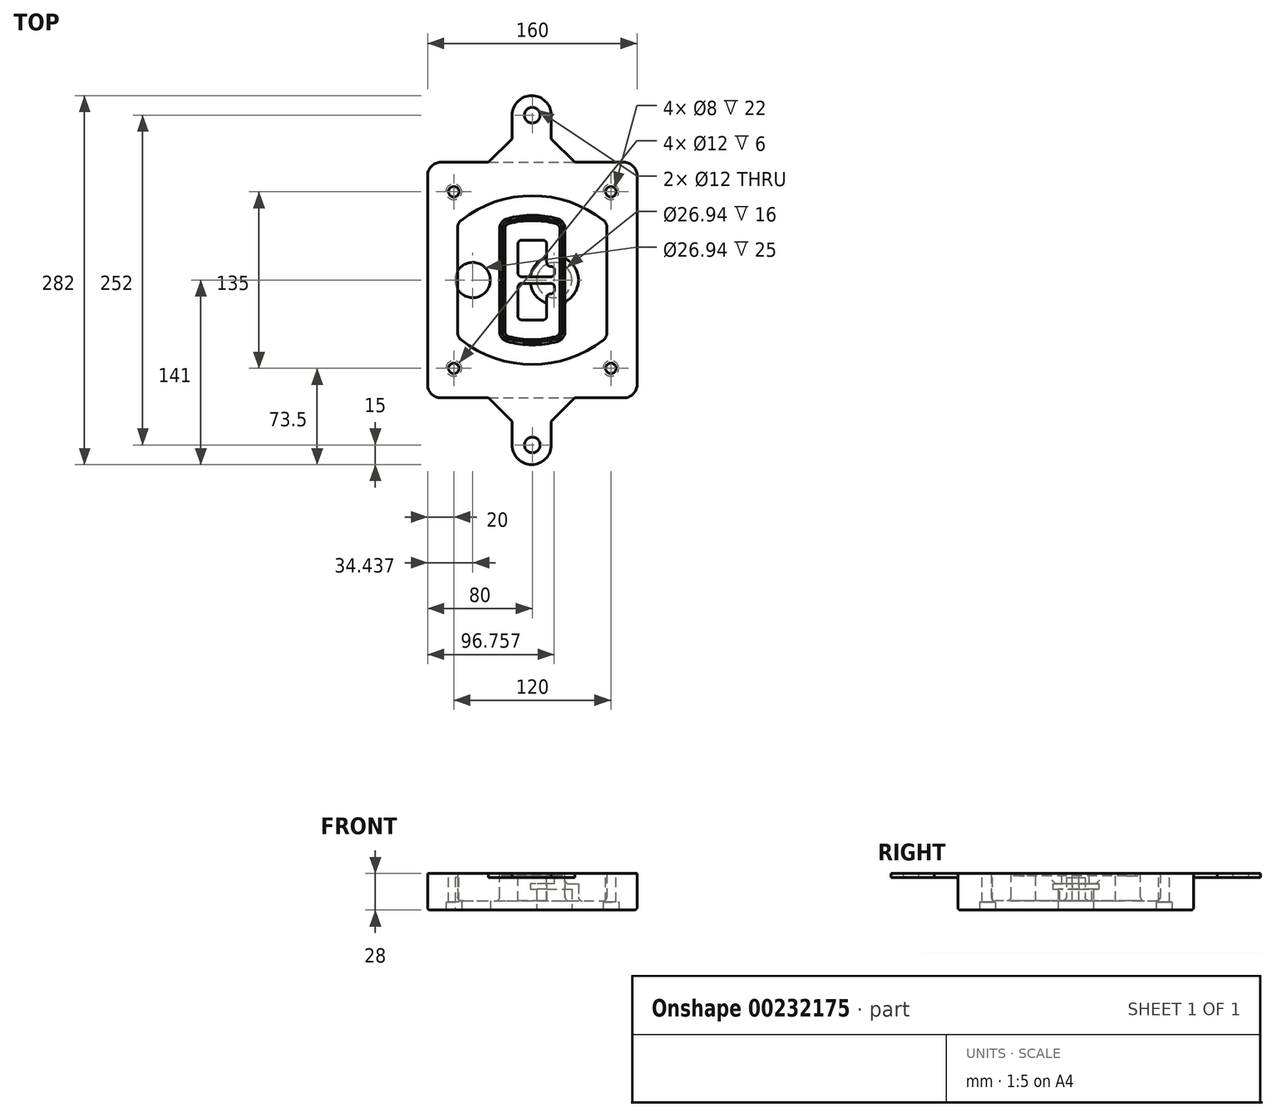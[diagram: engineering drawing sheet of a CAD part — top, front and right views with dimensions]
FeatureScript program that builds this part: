
annotation { "Feature Type Name" : "Feature", "Feature Type Description" : "" }
export const myFeature = defineFeature(function(context is Context, id is Id, definition is map)
    precondition{}
    {
        {
            var Q0;
            Q0=qCreatedBy(makeId("Top.planeOp"),FACE);
            var sketch = newSketch(context, id + "F0", { "sketchPlane" : qUnion([Q0])});
            skPoint(sketch, "E0.rect.middle", {"position": v(0, 0) * mm});
            skLineSegment(sketch, "E1.bottom", {"start": v(-70, -90) * mm, "end": v(70, -90) * mm});
            skLineSegment(sketch, "E1.top", {"start": v(-70, 90) * mm, "end": v(70, 90) * mm});
            skLineSegment(sketch, "E1.left", {"start": v(-80, -80) * mm, "end": v(-80, 80) * mm});
            skLineSegment(sketch, "E1.right", {"start": v(80, -80) * mm, "end": v(80, 80) * mm});
            skLineSegment(sketch, "E2", {"start": v(-80, 90) * mm, "end": v(80, -90) * mm, "construction": true});
            skLineSegment(sketch, "E3", {"start": v(80, 90) * mm, "end": v(-80, -90) * mm, "construction": true});
            skCircle(sketch, "E4", {"center": v(-60, 67.5) * mm, "radius": 4 * mm});
            skCircle(sketch, "E5", {"center": v(60, 67.5) * mm, "radius": 4 * mm});
            skCircle(sketch, "E6", {"center": v(60, -67.5) * mm, "radius": 4 * mm});
            skCircle(sketch, "E7", {"center": v(-60, -67.5) * mm, "radius": 4 * mm});
            skLineSegment(sketch, "E8", {"start": v(-60, 67.5) * mm, "end": v(60, 67.5) * mm, "construction": true});
            skLineSegment(sketch, "E9", {"start": v(60, 67.5) * mm, "end": v(60, -67.5) * mm, "construction": true});
            skLineSegment(sketch, "E10", {"start": v(60, -67.5) * mm, "end": v(-60, -67.5) * mm, "construction": true});
            skLineSegment(sketch, "E11", {"start": v(-60, -67.5) * mm, "end": v(-60, 67.5) * mm, "construction": true});
            skLineSegment(sketch, "E12", {"start": v(-60, 40.3) * mm, "end": v(-60, -40.3) * mm});
            skLineSegment(sketch, "E13", {"start": v(60, 40.3) * mm, "end": v(60, -40.3) * mm});
            skArc(sketch, "E14", {"start": v(56.15, 48.18) * mm, "mid": v(0, 67.5) * mm, "end": v(-56.15, 48.18) * mm});
            skArc(sketch, "E15", {"start": v(-56.15, -48.18) * mm, "mid": v(0, -67.5) * mm, "end": v(56.15, -48.18) * mm});
            skLineSegment(sketch, "E16", {"start": v(-60, 0) * mm, "end": v(60, 0) * mm, "construction": true});
            skPoint(sketch, "E17.visualSharp", {"position": v(-60, -45) * mm});
            skArc(sketch, "E17.filletArc", {"start": v(-60, -40.3) * mm, "mid": v(-58.99, -44.68) * mm, "end": v(-56.15, -48.18) * mm});
            skPoint(sketch, "E18.visualSharp", {"position": v(-60, 45) * mm});
            skArc(sketch, "E18.filletArc", {"start": v(-56.15, 48.18) * mm, "mid": v(-58.99, 44.68) * mm, "end": v(-60, 40.3) * mm});
            skPoint(sketch, "E19.visualSharp", {"position": v(60, 45) * mm});
            skArc(sketch, "E19.filletArc", {"start": v(60, 40.3) * mm, "mid": v(58.99, 44.68) * mm, "end": v(56.15, 48.18) * mm});
            skPoint(sketch, "E20.visualSharp", {"position": v(60, -45) * mm});
            skArc(sketch, "E20.filletArc", {"start": v(56.15, -48.18) * mm, "mid": v(58.99, -44.68) * mm, "end": v(60, -40.3) * mm});
            skPoint(sketch, "E21.visualSharp", {"position": v(-80, 90) * mm});
            skArc(sketch, "E21.filletArc", {"start": v(-70, 90) * mm, "mid": v(-77.07, 87.07) * mm, "end": v(-80, 80) * mm});
            skPoint(sketch, "E22.visualSharp", {"position": v(80, 90) * mm});
            skArc(sketch, "E22.filletArc", {"start": v(80, 80) * mm, "mid": v(77.07, 87.07) * mm, "end": v(70, 90) * mm});
            skPoint(sketch, "E23.visualSharp", {"position": v(80, -90) * mm});
            skArc(sketch, "E23.filletArc", {"start": v(70, -90) * mm, "mid": v(77.07, -87.07) * mm, "end": v(80, -80) * mm});
            skPoint(sketch, "E24.visualSharp", {"position": v(-80, -90) * mm});
            skArc(sketch, "E24.filletArc", {"start": v(-80, -80) * mm, "mid": v(-77.07, -87.07) * mm, "end": v(-70, -90) * mm});
            skArc(sketch, "E25.0", {"start": v(57, 40.3) * mm, "mid": v(56.3, 43.36) * mm, "end": v(54.3, 45.81) * mm});
            skLineSegment(sketch, "E25.1", {"start": v(57, 40.3) * mm, "end": v(57, -40.3) * mm});
            skArc(sketch, "E25.2", {"start": v(54.3, -45.81) * mm, "mid": v(56.3, -43.36) * mm, "end": v(57, -40.3) * mm});
            skArc(sketch, "E25.3", {"start": v(-54.3, -45.81) * mm, "mid": v(0, -64.5) * mm, "end": v(54.3, -45.81) * mm});
            skArc(sketch, "E25.4", {"start": v(-57, -40.3) * mm, "mid": v(-56.3, -43.36) * mm, "end": v(-54.3, -45.81) * mm});
            skArc(sketch, "E25.5", {"start": v(54.3, 45.81) * mm, "mid": v(0, 64.5) * mm, "end": v(-54.3, 45.81) * mm});
            skLineSegment(sketch, "E25.6", {"start": v(-57, 40.3) * mm, "end": v(-57, -40.3) * mm});
            skArc(sketch, "E25.7", {"start": v(-54.3, 45.81) * mm, "mid": v(-56.3, 43.36) * mm, "end": v(-57, 40.3) * mm});
            skArc(sketch, "E26.0", {"start": v(-58.62, 51.33) * mm, "mid": v(-62.58, 46.43) * mm, "end": v(-64, 40.3) * mm});
            skArc(sketch, "E26.1", {"start": v(58.62, 51.33) * mm, "mid": v(0, 71.5) * mm, "end": v(-58.62, 51.33) * mm});
            skArc(sketch, "E26.2", {"start": v(64, 40.3) * mm, "mid": v(62.58, 46.43) * mm, "end": v(58.62, 51.33) * mm});
            skLineSegment(sketch, "E26.3", {"start": v(64, 40.3) * mm, "end": v(64, -40.3) * mm});
            skArc(sketch, "E26.4", {"start": v(58.62, -51.33) * mm, "mid": v(62.58, -46.43) * mm, "end": v(64, -40.3) * mm});
            skLineSegment(sketch, "E26.5", {"start": v(-64, 40.3) * mm, "end": v(-64, -40.3) * mm});
            skArc(sketch, "E26.6", {"start": v(-58.62, -51.33) * mm, "mid": v(0, -71.5) * mm, "end": v(58.62, -51.33) * mm});
            skArc(sketch, "E26.7", {"start": v(-64, -40.3) * mm, "mid": v(-62.58, -46.43) * mm, "end": v(-58.62, -51.33) * mm});
            skSolve(sketch);
        }
        {
            var Q0;
            Q0=makeQuery(id+"F0.imprint","IMPRINT",FACE,{"disambiguationData":[TD([[makeQuery(id+"F0.imprint","IMPRINT",EDGE,{"derivedFrom":sQuery(id+"F0.wireOp",EDGE,"E1.bottom")}),1.0]])]});
            var Q1;
            Q1=makeQuery(id+"F0.imprint","IMPRINT",FACE,{"disambiguationData":[TD([[makeQuery(id+"F0.imprint","IMPRINT",EDGE,{"derivedFrom":sQuery(id+"F0.wireOp",EDGE,"E12")}),1.0]])]});
            var Q2;
            Q2=makeQuery(id+"F0.imprint","IMPRINT",FACE,{"disambiguationData":[TD([[makeQuery(id+"F0.imprint","IMPRINT",EDGE,{"derivedFrom":sQuery(id+"F0.wireOp",EDGE,"E25.0")}),1.0]])]});
            var Q3;
            Q3=makeQuery(id+"F0.imprint","IMPRINT",FACE,{"disambiguationData":[TD([[makeQuery(id+"F0.imprint","IMPRINT",EDGE,{"derivedFrom":sQuery(id+"F0.wireOp",EDGE,"E12")}),-1.0]])]});
            extrude(context, id + "F1", {"entities" : qUnion([Q0, Q1, Q2, Q3]), "oppositeDirection" : true, "depth" : 25 * mm});
        }
        {
            var Q0;
            Q0=makeQuery(id+"F0.imprint","IMPRINT",FACE,{"disambiguationData":[TD([[makeQuery(id+"F0.imprint","IMPRINT",EDGE,{"derivedFrom":sQuery(id+"F0.wireOp",EDGE,"E12")}),1.0]])]});
            extrude(context, id + "F2", {"entities" : qUnion([Q0]), "operationType" : NewBodyOperationType.ADD, "depth" : 3 * mm});
        }
        {
            var Q0;
            Q0=makeQuery(id+"F0.imprint","IMPRINT",FACE,{"disambiguationData":[TD([[makeQuery(id+"F0.imprint","IMPRINT",EDGE,{"derivedFrom":sQuery(id+"F0.wireOp",EDGE,"E25.0")}),1.0]])]});
            extrude(context, id + "F3", {"entities" : qUnion([Q0]), "operationType" : NewBodyOperationType.REMOVE, "oppositeDirection" : true, "depth" : 18 * mm});
        }
        {
            var Q0;
            Q0=makeQuery(id+"F2.opExtrude","CAP_FACE",FACE,{"disambiguationData":[OSD([sQuery(id+"F0.wireOp",EDGE,"E12"),sQuery(id+"F0.wireOp",EDGE,"E13"),sQuery(id+"F0.wireOp",EDGE,"E14"),sQuery(id+"F0.wireOp",EDGE,"E15"),sQuery(id+"F0.wireOp",EDGE,"E17.filletArc"),sQuery(id+"F0.wireOp",EDGE,"E18.filletArc"),sQuery(id+"F0.wireOp",EDGE,"E19.filletArc"),sQuery(id+"F0.wireOp",EDGE,"E20.filletArc"),sQuery(id+"F0.wireOp",EDGE,"E25.0"),sQuery(id+"F0.wireOp",EDGE,"E25.1"),sQuery(id+"F0.wireOp",EDGE,"E25.2"),sQuery(id+"F0.wireOp",EDGE,"E25.3"),sQuery(id+"F0.wireOp",EDGE,"E25.4"),sQuery(id+"F0.wireOp",EDGE,"E25.5"),sQuery(id+"F0.wireOp",EDGE,"E25.6"),sQuery(id+"F0.wireOp",EDGE,"E25.7")])],"isStart":false});
            var sketch = newSketch(context, id + "F4", { "sketchPlane" : qUnion([Q0])});
            skArc(sketch, "E27.0", {"start": v(-19.08, -46.97) * mm, "mid": v(0, -49.5) * mm, "end": v(19.08, -46.97) * mm});
            skArc(sketch, "E28.0", {"start": v(19.08, 46.97) * mm, "mid": v(0, 49.5) * mm, "end": v(-19.08, 46.97) * mm});
            skLineSegment(sketch, "E29", {"start": v(-25, 39.25) * mm, "end": v(-25, -39.25) * mm});
            skLineSegment(sketch, "E30", {"start": v(25, 39.25) * mm, "end": v(25, -39.25) * mm});
            skLineSegment(sketch, "E31", {"start": v(-25, 45.1) * mm, "end": v(25, 45.1) * mm, "construction": true});
            skLineSegment(sketch, "E32", {"start": v(-25, -45.1) * mm, "end": v(25, -45.1) * mm, "construction": true});
            skPoint(sketch, "E33.visualSharp", {"position": v(-25, 45.1) * mm});
            skArc(sketch, "E33.filletArc", {"start": v(-19.08, 46.97) * mm, "mid": v(-23.35, 44.11) * mm, "end": v(-25, 39.25) * mm});
            skPoint(sketch, "E34.visualSharp", {"position": v(25, 45.1) * mm});
            skArc(sketch, "E34.filletArc", {"start": v(25, 39.25) * mm, "mid": v(23.35, 44.11) * mm, "end": v(19.08, 46.97) * mm});
            skPoint(sketch, "E35.visualSharp", {"position": v(25, -45.1) * mm});
            skArc(sketch, "E35.filletArc", {"start": v(19.08, -46.97) * mm, "mid": v(23.35, -44.11) * mm, "end": v(25, -39.25) * mm});
            skPoint(sketch, "E36.visualSharp", {"position": v(-25, -45.1) * mm});
            skArc(sketch, "E36.filletArc", {"start": v(-25, -39.25) * mm, "mid": v(-23.35, -44.11) * mm, "end": v(-19.08, -46.97) * mm});
            skArc(sketch, "E37.0", {"start": v(54.3, 45.81) * mm, "mid": v(0, 64.5) * mm, "end": v(-54.3, 45.81) * mm});
            skArc(sketch, "E37.1", {"start": v(-54.3, 45.81) * mm, "mid": v(-56.3, 43.36) * mm, "end": v(-57, 40.3) * mm});
            skLineSegment(sketch, "E37.2", {"start": v(-57, 40.3) * mm, "end": v(-57, -40.3) * mm});
            skArc(sketch, "E37.3", {"start": v(-57, -40.3) * mm, "mid": v(-56.3, -43.36) * mm, "end": v(-54.3, -45.81) * mm});
            skArc(sketch, "E37.4", {"start": v(-54.3, -45.81) * mm, "mid": v(0, -64.5) * mm, "end": v(54.3, -45.81) * mm});
            skArc(sketch, "E37.5", {"start": v(54.3, -45.81) * mm, "mid": v(56.3, -43.36) * mm, "end": v(57, -40.3) * mm});
            skLineSegment(sketch, "E37.6", {"start": v(57, 40.3) * mm, "end": v(57, -40.3) * mm});
            skArc(sketch, "E37.7", {"start": v(57, 40.3) * mm, "mid": v(56.3, 43.36) * mm, "end": v(54.3, 45.81) * mm});
            skLineSegment(sketch, "E38.0", {"start": v(23, 39.25) * mm, "end": v(23, -39.25) * mm});
            skArc(sketch, "E38.1", {"start": v(18.56, -45.04) * mm, "mid": v(21.76, -42.9) * mm, "end": v(23, -39.25) * mm});
            skArc(sketch, "E38.2", {"start": v(-18.56, -45.04) * mm, "mid": v(0, -47.5) * mm, "end": v(18.56, -45.04) * mm});
            skArc(sketch, "E38.3", {"start": v(-23, -39.25) * mm, "mid": v(-21.76, -42.9) * mm, "end": v(-18.56, -45.04) * mm});
            skLineSegment(sketch, "E38.4", {"start": v(-23, 39.25) * mm, "end": v(-23, -39.25) * mm});
            skArc(sketch, "E38.5", {"start": v(23, 39.25) * mm, "mid": v(21.76, 42.9) * mm, "end": v(18.56, 45.04) * mm});
            skArc(sketch, "E38.6", {"start": v(-18.56, 45.04) * mm, "mid": v(-21.76, 42.9) * mm, "end": v(-23, 39.25) * mm});
            skArc(sketch, "E38.7", {"start": v(18.56, 45.04) * mm, "mid": v(0, 47.5) * mm, "end": v(-18.56, 45.04) * mm});
            skArc(sketch, "E39.0", {"start": v(21, 39.25) * mm, "mid": v(20.18, 41.68) * mm, "end": v(18.04, 43.1) * mm});
            skLineSegment(sketch, "E39.1", {"start": v(21, 39.25) * mm, "end": v(21, -39.25) * mm});
            skArc(sketch, "E39.2", {"start": v(18.04, -43.1) * mm, "mid": v(20.18, -41.68) * mm, "end": v(21, -39.25) * mm});
            skArc(sketch, "E39.3", {"start": v(-18.04, -43.1) * mm, "mid": v(0, -45.5) * mm, "end": v(18.04, -43.1) * mm});
            skArc(sketch, "E39.4", {"start": v(-21, -39.25) * mm, "mid": v(-20.18, -41.68) * mm, "end": v(-18.04, -43.1) * mm});
            skArc(sketch, "E39.5", {"start": v(18.04, 43.1) * mm, "mid": v(0, 45.5) * mm, "end": v(-18.04, 43.1) * mm});
            skLineSegment(sketch, "E39.6", {"start": v(-21, 39.25) * mm, "end": v(-21, -39.25) * mm});
            skArc(sketch, "E39.7", {"start": v(-18.04, 43.1) * mm, "mid": v(-20.18, 41.68) * mm, "end": v(-21, 39.25) * mm});
            skLineSegment(sketch, "E40", {"start": v(-25, 0) * mm, "end": v(25, 0) * mm, "construction": true});
            skLineSegment(sketch, "E41", {"start": v(-11, 5.5) * mm, "end": v(-11, 27.5) * mm});
            skLineSegment(sketch, "E42", {"start": v(-8, 30.5) * mm, "end": v(8, 30.5) * mm});
            skLineSegment(sketch, "E43", {"start": v(11, 27.5) * mm, "end": v(11, 13.5) * mm});
            skLineSegment(sketch, "E44", {"start": v(14, 10.5) * mm, "end": v(14, 10.5) * mm});
            skLineSegment(sketch, "E45", {"start": v(17, 7.5) * mm, "end": v(17, 5.5) * mm});
            skLineSegment(sketch, "E46", {"start": v(14, 2.5) * mm, "end": v(-8, 2.5) * mm});
            skPoint(sketch, "E47.visualSharp", {"position": v(-11, 30.5) * mm});
            skArc(sketch, "E47.filletArc", {"start": v(-8, 30.5) * mm, "mid": v(-10.12, 29.62) * mm, "end": v(-11, 27.5) * mm});
            skPoint(sketch, "E48.visualSharp", {"position": v(11, 30.5) * mm});
            skArc(sketch, "E48.filletArc", {"start": v(11, 27.5) * mm, "mid": v(10.12, 29.62) * mm, "end": v(8, 30.5) * mm});
            skPoint(sketch, "E49.visualSharp", {"position": v(11, 10.5) * mm});
            skArc(sketch, "E49.filletArc", {"start": v(11, 13.5) * mm, "mid": v(11.88, 11.38) * mm, "end": v(14, 10.5) * mm});
            skPoint(sketch, "E50.visualSharp", {"position": v(17, 10.5) * mm});
            skArc(sketch, "E50.filletArc", {"start": v(17, 7.5) * mm, "mid": v(16.12, 9.62) * mm, "end": v(14, 10.5) * mm});
            skPoint(sketch, "E51.visualSharp", {"position": v(17, 2.5) * mm});
            skArc(sketch, "E51.filletArc", {"start": v(14, 2.5) * mm, "mid": v(16.12, 3.38) * mm, "end": v(17, 5.5) * mm});
            skPoint(sketch, "E52.visualSharp", {"position": v(-11, 2.5) * mm});
            skArc(sketch, "E52.filletArc", {"start": v(-11, 5.5) * mm, "mid": v(-10.12, 3.38) * mm, "end": v(-8, 2.5) * mm});
            skLineSegment(sketch, "E53.0.MirrorCS", {"start": v(14, -2.5) * mm, "end": v(-8, -2.5) * mm});
            skArc(sketch, "E54.0.MirrorCS", {"start": v(-11, -5.5) * mm, "mid": v(-10.12, -3.38) * mm, "end": v(-8, -2.5) * mm});
            skLineSegment(sketch, "E55.0.MirrorCS", {"start": v(-11, -5.5) * mm, "end": v(-11, -27.5) * mm});
            skArc(sketch, "E56.0.MirrorCS", {"start": v(-8, -30.5) * mm, "mid": v(-10.12, -29.62) * mm, "end": v(-11, -27.5) * mm});
            skLineSegment(sketch, "E57.0.MirrorCS", {"start": v(-8, -30.5) * mm, "end": v(8, -30.5) * mm});
            skArc(sketch, "E58.0.MirrorCS", {"start": v(11, -27.5) * mm, "mid": v(10.12, -29.62) * mm, "end": v(8, -30.5) * mm});
            skLineSegment(sketch, "E59.0.MirrorCS", {"start": v(11, -27.5) * mm, "end": v(11, -13.5) * mm});
            skArc(sketch, "E60.0.MirrorCS", {"start": v(11, -13.5) * mm, "mid": v(11.88, -11.38) * mm, "end": v(14, -10.5) * mm});
            skArc(sketch, "E61.0.MirrorCS", {"start": v(17, -7.5) * mm, "mid": v(16.12, -9.62) * mm, "end": v(14, -10.5) * mm});
            skLineSegment(sketch, "E62.0.MirrorCS", {"start": v(17, -7.5) * mm, "end": v(17, -5.5) * mm});
            skArc(sketch, "E63.0.MirrorCS", {"start": v(14, -2.5) * mm, "mid": v(16.12, -3.38) * mm, "end": v(17, -5.5) * mm});
            skSolve(sketch);
        }
        {
            var Q0;
            Q0=makeQuery(id+"F4.imprint","IMPRINT",FACE,{"disambiguationData":[TD([[makeQuery(id+"F4.imprint","IMPRINT",EDGE,{"derivedFrom":sQuery(id+"F4.wireOp",EDGE,"E27.0")}),1.0]])]});
            var Q1;
            Q1=makeQuery(id+"F4.imprint","IMPRINT",FACE,{"disambiguationData":[TD([[makeQuery(id+"F4.imprint","IMPRINT",EDGE,{"derivedFrom":sQuery(id+"F4.wireOp",EDGE,"E38.0")}),-1.0]])]});
            var Q2;
            Q2=makeQuery(id+"F4.imprint","IMPRINT",FACE,{"disambiguationData":[TD([[makeQuery(id+"F4.imprint","IMPRINT",EDGE,{"derivedFrom":sQuery(id+"F4.wireOp",EDGE,"E39.0")}),1.0]])]});
            extrude(context, id + "F5", {"entities" : qUnion([Q0, Q1, Q2]), "operationType" : NewBodyOperationType.ADD, "endBound" : BoundingType.UP_TO_NEXT, "oppositeDirection" : true, "depth" : 25 * mm});
        }
        {
            var Q0;
            Q0=makeQuery(id+"F4.imprint","IMPRINT",FACE,{"disambiguationData":[TD([[makeQuery(id+"F4.imprint","IMPRINT",EDGE,{"derivedFrom":sQuery(id+"F4.wireOp",EDGE,"E38.0")}),-1.0]])]});
            extrude(context, id + "F6", {"entities" : qUnion([Q0]), "operationType" : NewBodyOperationType.REMOVE, "oppositeDirection" : true, "depth" : 2 * mm});
        }
        {
            var Q0;
            Q0=makeQuery(id+"F1.opExtrude","CAP_FACE",FACE,{"disambiguationData":[OSD([sQuery(id+"F0.wireOp",EDGE,"E1.bottom"),sQuery(id+"F0.wireOp",EDGE,"E1.top"),sQuery(id+"F0.wireOp",EDGE,"E1.left"),sQuery(id+"F0.wireOp",EDGE,"E1.right"),sQuery(id+"F0.wireOp",EDGE,"E4"),sQuery(id+"F0.wireOp",EDGE,"E5"),sQuery(id+"F0.wireOp",EDGE,"E6"),sQuery(id+"F0.wireOp",EDGE,"E7"),sQuery(id+"F0.wireOp",EDGE,"E21.filletArc"),sQuery(id+"F0.wireOp",EDGE,"E22.filletArc"),sQuery(id+"F0.wireOp",EDGE,"E23.filletArc"),sQuery(id+"F0.wireOp",EDGE,"E24.filletArc")])],"isStart":false});
            var sketch = newSketch(context, id + "F7", { "sketchPlane" : qUnion([Q0])});
            skCircle(sketch, "E64", {"center": v(16.76, 0) * mm, "radius": 13.47 * mm});
            skCircle(sketch, "E65", {"center": v(-45.56, 0) * mm, "radius": 13.47 * mm});
            skLineSegment(sketch, "E66", {"start": v(80, 0) * mm, "end": v(-80, 0) * mm});
            skCircle(sketch, "E67", {"center": v(16.76, 0) * mm, "radius": 18.47 * mm});
            skCircle(sketch, "E68", {"center": v(60, -67.5) * mm, "radius": 6 * mm});
            skCircle(sketch, "E69", {"center": v(-60, -67.5) * mm, "radius": 6 * mm});
            skCircle(sketch, "E70", {"center": v(-60, 67.5) * mm, "radius": 6 * mm});
            skCircle(sketch, "E71", {"center": v(60, 67.5) * mm, "radius": 6 * mm});
            skSolve(sketch);
        }
        {
            var Q0;
            {var subQ1=sQuery(id+"F7.wireOp",EDGE,"E66");var subQ4=sQuery(id+"F7.wireOp",EDGE,"E64");var subQ6=makeQuery(id+"F7.imprint","INTERSECT",VERTEX,{"disambiguationData":[OD(0.0)],"derivedFrom":[subQ4,subQ1]});Q0=makeQuery(id+"F7.imprint","IMPRINT",FACE,{"disambiguationData":[TD([[makeQuery(id+"F7.imprint","IMPRINT",EDGE,{"disambiguationData":[TD([[subQ6,-1.0]])],"derivedFrom":subQ4}),-1.0]])]});}
            var Q1;
            {var subQ0=sQuery(id+"F7.wireOp",EDGE,"E66");var subQ1=sQuery(id+"F7.wireOp",EDGE,"E64");var subQ3=makeQuery(id+"F7.imprint","INTERSECT",VERTEX,{"disambiguationData":[OD(0.0)],"derivedFrom":[subQ1,subQ0]});Q1=makeQuery(id+"F7.imprint","IMPRINT",FACE,{"disambiguationData":[TD([[makeQuery(id+"F7.imprint","IMPRINT",EDGE,{"disambiguationData":[TD([[subQ3,-1.0]])],"derivedFrom":subQ1}),1.0]])]});}
            var Q2;
            {var subQ0=sQuery(id+"F7.wireOp",EDGE,"E66");var subQ1=sQuery(id+"F7.wireOp",EDGE,"E64");var subQ3=makeQuery(id+"F7.imprint","INTERSECT",VERTEX,{"disambiguationData":[OD(0.0)],"derivedFrom":[subQ1,subQ0]});Q2=makeQuery(id+"F7.imprint","IMPRINT",FACE,{"disambiguationData":[TD([[makeQuery(id+"F7.imprint","IMPRINT",EDGE,{"disambiguationData":[TD([[subQ3,1.0]])],"derivedFrom":subQ1}),1.0]])]});}
            var Q3;
            {var subQ1=sQuery(id+"F7.wireOp",EDGE,"E66");var subQ4=sQuery(id+"F7.wireOp",EDGE,"E64");var subQ6=makeQuery(id+"F7.imprint","INTERSECT",VERTEX,{"disambiguationData":[OD(0.0)],"derivedFrom":[subQ4,subQ1]});Q3=makeQuery(id+"F7.imprint","IMPRINT",FACE,{"disambiguationData":[TD([[makeQuery(id+"F7.imprint","IMPRINT",EDGE,{"disambiguationData":[TD([[subQ6,1.0]])],"derivedFrom":subQ4}),-1.0]])]});}
            extrude(context, id + "F8", {"entities" : qUnion([Q0, Q1, Q2, Q3]), "operationType" : NewBodyOperationType.ADD, "oppositeDirection" : true, "depth" : 20 * mm});
        }
        {
            var Q0;
            {var subQ0=sQuery(id+"F7.wireOp",EDGE,"E66");var subQ1=sQuery(id+"F7.wireOp",EDGE,"E64");var subQ3=makeQuery(id+"F7.imprint","INTERSECT",VERTEX,{"disambiguationData":[OD(0.0)],"derivedFrom":[subQ1,subQ0]});Q0=makeQuery(id+"F7.imprint","IMPRINT",FACE,{"disambiguationData":[TD([[makeQuery(id+"F7.imprint","IMPRINT",EDGE,{"disambiguationData":[TD([[subQ3,-1.0]])],"derivedFrom":subQ1}),1.0]])]});}
            var Q1;
            {var subQ0=sQuery(id+"F7.wireOp",EDGE,"E66");var subQ1=sQuery(id+"F7.wireOp",EDGE,"E64");var subQ3=makeQuery(id+"F7.imprint","INTERSECT",VERTEX,{"disambiguationData":[OD(0.0)],"derivedFrom":[subQ1,subQ0]});Q1=makeQuery(id+"F7.imprint","IMPRINT",FACE,{"disambiguationData":[TD([[makeQuery(id+"F7.imprint","IMPRINT",EDGE,{"disambiguationData":[TD([[subQ3,1.0]])],"derivedFrom":subQ1}),1.0]])]});}
            extrude(context, id + "F9", {"entities" : qUnion([Q0, Q1]), "operationType" : NewBodyOperationType.REMOVE, "oppositeDirection" : true, "depth" : 16 * mm});
        }
        {
            var Q0;
            {var subQ0=sQuery(id+"F7.wireOp",EDGE,"E66");var subQ1=sQuery(id+"F7.wireOp",EDGE,"E65");var subQ3=makeQuery(id+"F7.imprint","INTERSECT",VERTEX,{"disambiguationData":[OD(0.0)],"derivedFrom":[subQ1,subQ0]});Q0=makeQuery(id+"F7.imprint","IMPRINT",FACE,{"disambiguationData":[TD([[makeQuery(id+"F7.imprint","IMPRINT",EDGE,{"disambiguationData":[TD([[subQ3,-1.0]])],"derivedFrom":subQ1}),1.0]])]});}
            var Q1;
            {var subQ0=sQuery(id+"F7.wireOp",EDGE,"E66");var subQ1=sQuery(id+"F7.wireOp",EDGE,"E65");var subQ3=makeQuery(id+"F7.imprint","INTERSECT",VERTEX,{"disambiguationData":[OD(0.0)],"derivedFrom":[subQ1,subQ0]});Q1=makeQuery(id+"F7.imprint","IMPRINT",FACE,{"disambiguationData":[TD([[makeQuery(id+"F7.imprint","IMPRINT",EDGE,{"disambiguationData":[TD([[subQ3,1.0]])],"derivedFrom":subQ1}),1.0]])]});}
            extrude(context, id + "F10", {"entities" : qUnion([Q0, Q1]), "operationType" : NewBodyOperationType.REMOVE, "oppositeDirection" : true, "depth" : 25 * mm});
        }
        {
            var Q0;
            Q0=makeQuery(id+"F7.imprint","IMPRINT",FACE,{"disambiguationData":[TD([[makeQuery(id+"F7.imprint","IMPRINT",EDGE,{"derivedFrom":sQuery(id+"F7.wireOp",EDGE,"E68")}),1.0]])]});
            var Q1;
            Q1=makeQuery(id+"F7.imprint","IMPRINT",FACE,{"disambiguationData":[TD([[makeQuery(id+"F7.imprint","IMPRINT",EDGE,{"derivedFrom":makeQuery(id+"F1.opExtrude","CAP_EDGE",EDGE,{"disambiguationData":[OSD([sQuery(id+"F0.wireOp",EDGE,"E5")])],"isStart":false})}),-1.0]])]});
            var Q2;
            Q2=makeQuery(id+"F7.imprint","IMPRINT",FACE,{"disambiguationData":[TD([[makeQuery(id+"F7.imprint","IMPRINT",EDGE,{"derivedFrom":sQuery(id+"F7.wireOp",EDGE,"E69")}),1.0]])]});
            var Q3;
            Q3=makeQuery(id+"F7.imprint","IMPRINT",FACE,{"disambiguationData":[TD([[makeQuery(id+"F7.imprint","IMPRINT",EDGE,{"derivedFrom":makeQuery(id+"F1.opExtrude","CAP_EDGE",EDGE,{"disambiguationData":[OSD([sQuery(id+"F0.wireOp",EDGE,"E4")])],"isStart":false})}),-1.0]])]});
            var Q4;
            Q4=makeQuery(id+"F7.imprint","IMPRINT",FACE,{"disambiguationData":[TD([[makeQuery(id+"F7.imprint","IMPRINT",EDGE,{"derivedFrom":sQuery(id+"F7.wireOp",EDGE,"E70")}),1.0]])]});
            var Q5;
            Q5=makeQuery(id+"F7.imprint","IMPRINT",FACE,{"disambiguationData":[TD([[makeQuery(id+"F7.imprint","IMPRINT",EDGE,{"derivedFrom":makeQuery(id+"F1.opExtrude","CAP_EDGE",EDGE,{"disambiguationData":[OSD([sQuery(id+"F0.wireOp",EDGE,"E7")])],"isStart":false})}),-1.0]])]});
            var Q6;
            Q6=makeQuery(id+"F7.imprint","IMPRINT",FACE,{"disambiguationData":[TD([[makeQuery(id+"F7.imprint","IMPRINT",EDGE,{"derivedFrom":sQuery(id+"F7.wireOp",EDGE,"E71")}),1.0]])]});
            var Q7;
            Q7=makeQuery(id+"F7.imprint","IMPRINT",FACE,{"disambiguationData":[TD([[makeQuery(id+"F7.imprint","IMPRINT",EDGE,{"derivedFrom":makeQuery(id+"F1.opExtrude","CAP_EDGE",EDGE,{"disambiguationData":[OSD([sQuery(id+"F0.wireOp",EDGE,"E6")])],"isStart":false})}),-1.0]])]});
            extrude(context, id + "F11", {"entities" : qUnion([Q0, Q1, Q2, Q3, Q4, Q5, Q6, Q7]), "operationType" : NewBodyOperationType.REMOVE, "oppositeDirection" : true, "depth" : 6 * mm});
        }
        {
            var Q0;
            Q0=makeQuery(id+"F9.boolean.opBoolean","COPY",FACE,{"derivedFrom":makeQuery(id+"F9.opExtrude","CAP_FACE",FACE,{"disambiguationData":[OSD([sQuery(id+"F7.wireOp",EDGE,"E64")])],"isStart":false})});
            var sketch = newSketch(context, id + "F12", { "sketchPlane" : qUnion([Q0])});
            skArc(sketch, "E72.0", {"start": v(11, 17.55) * mm, "mid": v(2.57, 11.82) * mm, "end": v(-1.54, 2.5) * mm});
            skArc(sketch, "E72.1", {"start": v(-1.54, -2.5) * mm, "mid": v(2.57, -11.82) * mm, "end": v(11, -17.55) * mm});
            skLineSegment(sketch, "E73", {"start": v(-1.54, -2.5) * mm, "end": v(14, -2.5) * mm});
            skLineSegment(sketch, "E74.0", {"start": v(14, 2.5) * mm, "end": v(-1.54, 2.5) * mm});
            skArc(sketch, "E74.1", {"start": v(14, 2.5) * mm, "mid": v(16.12, 3.38) * mm, "end": v(17, 5.5) * mm});
            skLineSegment(sketch, "E74.2", {"start": v(17, 7.5) * mm, "end": v(17, 5.5) * mm});
            skArc(sketch, "E74.3", {"start": v(17, 7.5) * mm, "mid": v(16.12, 9.62) * mm, "end": v(14, 10.5) * mm});
            skArc(sketch, "E74.4", {"start": v(11, 13.5) * mm, "mid": v(11.88, 11.38) * mm, "end": v(14, 10.5) * mm});
            skLineSegment(sketch, "E74.5", {"start": v(11, 17.55) * mm, "end": v(11, 13.5) * mm});
            skLineSegment(sketch, "E74.7", {"start": v(14, -2.5) * mm, "end": v(-1.54, -2.5) * mm});
            skArc(sketch, "E74.8", {"start": v(14, -2.5) * mm, "mid": v(16.12, -3.38) * mm, "end": v(17, -5.5) * mm});
            skLineSegment(sketch, "E74.9", {"start": v(17, -7.5) * mm, "end": v(17, -5.5) * mm});
            skArc(sketch, "E74.10", {"start": v(17, -7.5) * mm, "mid": v(16.12, -9.62) * mm, "end": v(14, -10.5) * mm});
            skArc(sketch, "E74.11", {"start": v(11, -13.5) * mm, "mid": v(11.88, -11.38) * mm, "end": v(14, -10.5) * mm});
            skLineSegment(sketch, "E74.12", {"start": v(11, -17.55) * mm, "end": v(11, -13.5) * mm});
            skPoint(sketch, "E75.orphan", {"position": v(11, -27.5) * mm});
            skPoint(sketch, "E76.orphan", {"position": v(-8, -2.5) * mm});
            skPoint(sketch, "E77.orphan", {"position": v(-8, 2.5) * mm});
            skPoint(sketch, "E78.orphan", {"position": v(11, 27.5) * mm});
            skSolve(sketch);
        }
        {
            var Q0;
            {var subQ7=sQuery(id+"F12.wireOp",EDGE,"E72.0");var subQ14=sQuery(id+"F12.wireOp",EDGE,"E72.1");var subQ16=sQuery(id+"F12.wireOp",EDGE,"E74.1");var subQ18=sQuery(id+"F12.wireOp",EDGE,"E74.8");Q0=qUnion([makeQuery(id+"F12.imprint","IMPRINT",FACE,{"disambiguationData":[TD([[makeQuery(id+"F12.imprint","IMPRINT",EDGE,{"derivedFrom":subQ7}),1.0]])]}),makeQuery(id+"F12.imprint","IMPRINT",FACE,{"disambiguationData":[TD([[makeQuery(id+"F12.imprint","IMPRINT",EDGE,{"derivedFrom":subQ14}),1.0]])]}),makeQuery(id+"F12.imprint","IMPRINT",FACE,{"disambiguationData":[TD([[makeQuery(id+"F12.imprint","IMPRINT",EDGE,{"derivedFrom":subQ16}),1.0]])]}),makeQuery(id+"F12.imprint","IMPRINT",FACE,{"disambiguationData":[TD([[makeQuery(id+"F12.imprint","IMPRINT",EDGE,{"derivedFrom":subQ18}),-1.0]])]})]);}
            var Q1;
            Q1=makeQuery(id+"F5.boolean.opBoolean","SPLIT",FACE,{"disambiguationData":[TD([makeQuery(id+"F5.opExtrude","SWEPT_FACE",FACE,{"disambiguationData":[OSD([sQuery(id+"F4.wireOp",EDGE,"E41")])]})])],"derivedFrom":makeQuery(id+"F3.boolean.opBoolean","COPY",FACE,{"derivedFrom":makeQuery(id+"F3.opExtrude","CAP_FACE",FACE,{"disambiguationData":[OSD([sQuery(id+"F0.wireOp",EDGE,"E25.0"),sQuery(id+"F0.wireOp",EDGE,"E25.1"),sQuery(id+"F0.wireOp",EDGE,"E25.2"),sQuery(id+"F0.wireOp",EDGE,"E25.3"),sQuery(id+"F0.wireOp",EDGE,"E25.4"),sQuery(id+"F0.wireOp",EDGE,"E25.5"),sQuery(id+"F0.wireOp",EDGE,"E25.6"),sQuery(id+"F0.wireOp",EDGE,"E25.7")])],"isStart":false})})});
            extrude(context, id + "F13", {"entities" : qUnion([Q0]), "operationType" : NewBodyOperationType.REMOVE, "endBound" : BoundingType.UP_TO_SURFACE, "endBoundEntityFace" : qUnion([Q1]), "depth" : 25 * mm});
        }
        {
            var Q0;
            Q0=makeQuery(id+"F3.boolean.opBoolean","COPY",EDGE,{"derivedFrom":makeQuery(id+"F3.opExtrude","CAP_EDGE",EDGE,{"disambiguationData":[OSD([sQuery(id+"F0.wireOp",EDGE,"E25.6")])],"isStart":false})});
            var Q1;
            Q1=makeQuery(id+"F8.boolean.opBoolean","INTERSECT",EDGE,{"derivedFrom":[makeQuery(id+"F5.opExtrude","SWEPT_FACE",FACE,{"disambiguationData":[OSD([sQuery(id+"F4.wireOp",EDGE,"E30")])]}),makeQuery(id+"F8.opExtrude","CAP_FACE",FACE,{"disambiguationData":[OSD([sQuery(id+"F7.wireOp",EDGE,"E67")])],"isStart":false})]});
            var Q2;
            Q2=makeQuery(id+"F8.boolean.opBoolean","INTERSECT",EDGE,{"disambiguationData":[OD(1.0)],"derivedFrom":[makeQuery(id+"F5.opExtrude","SWEPT_FACE",FACE,{"disambiguationData":[OSD([sQuery(id+"F4.wireOp",EDGE,"E30")])]}),makeQuery(id+"F8.opExtrude","SWEPT_FACE",FACE,{"disambiguationData":[OSD([sQuery(id+"F7.wireOp",EDGE,"E67")])]})]});
            var Q3;
            {var subQ0=sQuery(id+"F4.wireOp",EDGE,"E30");Q3=makeQuery(id+"F8.boolean.opBoolean","SPLIT",EDGE,{"disambiguationData":[TD([makeQuery(id+"F5.opExtrude","SWEPT_FACE",FACE,{"disambiguationData":[OSD([sQuery(id+"F4.wireOp",EDGE,"E35.filletArc")])]})])],"derivedFrom":makeQuery(id+"F5.opExtrude","CAP_EDGE",EDGE,{"disambiguationData":[OSD([subQ0])],"isStart":false})});}
            var Q4;
            {var subQ0=sQuery(id+"F0.wireOp",EDGE,"E25.7");var subQ1=sQuery(id+"F0.wireOp",EDGE,"E25.1");var subQ2=sQuery(id+"F0.wireOp",EDGE,"E25.6");var subQ3=sQuery(id+"F0.wireOp",EDGE,"E25.5");var subQ4=sQuery(id+"F0.wireOp",EDGE,"E25.4");var subQ5=sQuery(id+"F0.wireOp",EDGE,"E25.0");var subQ6=sQuery(id+"F0.wireOp",EDGE,"E25.2");var subQ7=sQuery(id+"F0.wireOp",EDGE,"E25.3");Q4=makeQuery(id+"F8.boolean.opBoolean","INTERSECT",EDGE,{"derivedFrom":[makeQuery(id+"F5.boolean.opBoolean","SPLIT",FACE,{"disambiguationData":[TD([makeQuery(id+"F2.opExtrude","SWEPT_FACE",FACE,{"disambiguationData":[OSD([subQ5])]})])],"derivedFrom":makeQuery(id+"F3.boolean.opBoolean","COPY",FACE,{"derivedFrom":makeQuery(id+"F3.opExtrude","CAP_FACE",FACE,{"disambiguationData":[OSD([subQ5,subQ1,subQ6,subQ7,subQ4,subQ3,subQ2,subQ0])],"isStart":false})})}),makeQuery(id+"F8.opExtrude","SWEPT_FACE",FACE,{"disambiguationData":[OSD([sQuery(id+"F7.wireOp",EDGE,"E67")])]})]});}
            var Q5;
            Q5=makeQuery(id+"F8.boolean.opBoolean","INTERSECT",EDGE,{"disambiguationData":[OD(0.0)],"derivedFrom":[makeQuery(id+"F5.opExtrude","SWEPT_FACE",FACE,{"disambiguationData":[OSD([sQuery(id+"F4.wireOp",EDGE,"E30")])]}),makeQuery(id+"F8.opExtrude","SWEPT_FACE",FACE,{"disambiguationData":[OSD([sQuery(id+"F7.wireOp",EDGE,"E67")])]})]});
            fillet(context, id + "F14", {"entities" : qUnion([Q0, Q1, Q2, Q3, Q4, Q5]), "radius" : 3 * mm, "tangentPropagation" : true, "allowEdgeOverflow" : false});
        }
        {
            var Q0;
            Q0=makeQuery(id+"F1.opExtrude","CAP_EDGE",EDGE,{"disambiguationData":[OSD([sQuery(id+"F0.wireOp",EDGE,"E1.bottom")])],"isStart":false});
            fillet(context, id + "F15", {"entities" : qUnion([Q0]), "radius" : 2 * mm, "tangentPropagation" : true, "allowEdgeOverflow" : false});
        }
        {
            var Q0;
            {var subQ0=sQuery(id+"F0.wireOp",EDGE,"E22.filletArc");var subQ1=sQuery(id+"F0.wireOp",EDGE,"E7");var subQ2=sQuery(id+"F0.wireOp",EDGE,"E6");var subQ3=sQuery(id+"F0.wireOp",EDGE,"E5");var subQ4=sQuery(id+"F0.wireOp",EDGE,"E4");var subQ5=sQuery(id+"F0.wireOp",EDGE,"E1.bottom");var subQ6=sQuery(id+"F0.wireOp",EDGE,"E21.filletArc");var subQ7=sQuery(id+"F0.wireOp",EDGE,"E1.top");var subQ8=sQuery(id+"F0.wireOp",EDGE,"E1.left");var subQ9=sQuery(id+"F0.wireOp",EDGE,"E1.right");var subQ10=sQuery(id+"F0.wireOp",EDGE,"E23.filletArc");var subQ11=sQuery(id+"F0.wireOp",EDGE,"E24.filletArc");Q0=makeQuery(id+"F2.boolean.opBoolean","SPLIT",FACE,{"disambiguationData":[TD([makeQuery(id+"F1.opExtrude","SWEPT_FACE",FACE,{"disambiguationData":[OSD([subQ5])]})])],"derivedFrom":makeQuery(id+"F1.opExtrude","CAP_FACE",FACE,{"disambiguationData":[OSD([subQ5,subQ7,subQ8,subQ9,subQ4,subQ3,subQ2,subQ1,subQ6,subQ0,subQ10,subQ11])],"isStart":true})});}
            var sketch = newSketch(context, id + "F16", { "sketchPlane" : qUnion([Q0])});
            skArc(sketch, "E79.0", {"start": v(-56.15, 48.18) * mm, "mid": v(-58.99, 44.68) * mm, "end": v(-60, 40.3) * mm});
            skArc(sketch, "E79.1", {"start": v(56.15, 48.18) * mm, "mid": v(0, 67.5) * mm, "end": v(-56.15, 48.18) * mm});
            skArc(sketch, "E79.2", {"start": v(60, 40.3) * mm, "mid": v(58.99, 44.68) * mm, "end": v(56.15, 48.18) * mm});
            skLineSegment(sketch, "E79.3", {"start": v(60, 40.3) * mm, "end": v(60, -40.3) * mm});
            skArc(sketch, "E79.4", {"start": v(56.15, -48.18) * mm, "mid": v(58.99, -44.68) * mm, "end": v(60, -40.3) * mm});
            skArc(sketch, "E79.5", {"start": v(-56.15, -48.18) * mm, "mid": v(0, -67.5) * mm, "end": v(56.15, -48.18) * mm});
            skArc(sketch, "E79.6", {"start": v(-60, -40.3) * mm, "mid": v(-58.99, -44.68) * mm, "end": v(-56.15, -48.18) * mm});
            skLineSegment(sketch, "E79.7", {"start": v(-60, 40.3) * mm, "end": v(-60, -40.3) * mm});
            skLineSegment(sketch, "E79.8", {"start": v(-80, -80) * mm, "end": v(-80, 80) * mm});
            skArc(sketch, "E79.9", {"start": v(-80, -80) * mm, "mid": v(-77.07, -87.07) * mm, "end": v(-70, -90) * mm});
            skLineSegment(sketch, "E79.10", {"start": v(-70, -90) * mm, "end": v(70, -90) * mm});
            skArc(sketch, "E79.11", {"start": v(70, -90) * mm, "mid": v(77.07, -87.07) * mm, "end": v(80, -80) * mm});
            skLineSegment(sketch, "E79.12", {"start": v(80, -80) * mm, "end": v(80, 80) * mm});
            skArc(sketch, "E79.13", {"start": v(80, 80) * mm, "mid": v(77.07, 87.07) * mm, "end": v(70, 90) * mm});
            skLineSegment(sketch, "E79.14", {"start": v(-70, 90) * mm, "end": v(70, 90) * mm});
            skArc(sketch, "E79.15", {"start": v(-70, 90) * mm, "mid": v(-77.07, 87.07) * mm, "end": v(-80, 80) * mm});
            skCircle(sketch, "E79.16", {"center": v(60, -67.5) * mm, "radius": 4 * mm});
            skCircle(sketch, "E79.17", {"center": v(-60, -67.5) * mm, "radius": 4 * mm});
            skCircle(sketch, "E79.18", {"center": v(-60, 67.5) * mm, "radius": 4 * mm});
            skCircle(sketch, "E79.19", {"center": v(60, 67.5) * mm, "radius": 4 * mm});
            skLineSegment(sketch, "E80", {"start": v(0, 90) * mm, "end": v(0, 126) * mm, "construction": true});
            skLineSegment(sketch, "E81", {"start": v(-33.52, 90) * mm, "end": v(-15.52, 108) * mm});
            skLineSegment(sketch, "E82", {"start": v(-15.52, 108) * mm, "end": v(-15.52, 126) * mm});
            skLineSegment(sketch, "E83", {"start": v(32.48, 90) * mm, "end": v(14.48, 108) * mm});
            skPoint(sketch, "E83.endSnap0", {"position": v(0, 108) * mm});
            skLineSegment(sketch, "E84", {"start": v(14.48, 108) * mm, "end": v(14.48, 126) * mm});
            skArc(sketch, "E85", {"start": v(14.48, 126) * mm, "mid": v(-0.52, 141) * mm, "end": v(-15.52, 126) * mm});
            skCircle(sketch, "E86", {"center": v(0, 126) * mm, "radius": 6 * mm});
            skLineSegment(sketch, "E87", {"start": v(80, 0) * mm, "end": v(-98.56, 0) * mm});
            skPoint(sketch, "E87.endSnap0", {"position": v(-80, 0) * mm});
            skLineSegment(sketch, "E88", {"start": v(-98.56, 0) * mm, "end": v(91.7, 0) * mm, "construction": true});
            skLineSegment(sketch, "E89.MirrorCS", {"start": v(-15.52, -108) * mm, "end": v(-15.52, -126) * mm});
            skLineSegment(sketch, "E90.MirrorCS", {"start": v(-33.52, -90) * mm, "end": v(-15.52, -108) * mm});
            skArc(sketch, "E91.MirrorCS", {"start": v(14.48, -126) * mm, "mid": v(-0.52, -141) * mm, "end": v(-15.52, -126) * mm});
            skLineSegment(sketch, "E92.MirrorCS", {"start": v(14.48, -108) * mm, "end": v(14.48, -126) * mm});
            skLineSegment(sketch, "E93.MirrorCS", {"start": v(32.48, -90) * mm, "end": v(14.48, -108) * mm});
            skLineSegment(sketch, "E94.MirrorCS", {"start": v(0, -90) * mm, "end": v(0, -126) * mm, "construction": true});
            skCircle(sketch, "E95.MirrorC", {"center": v(0, -126) * mm, "radius": 6 * mm});
            skSolve(sketch);
        }
        {
            var Q0;
            {var subQ1=sQuery(id+"F16.wireOp",EDGE,"E81");Q0=makeQuery(id+"F16.imprint","IMPRINT",FACE,{"disambiguationData":[TD([[makeQuery(id+"F16.imprint","IMPRINT",EDGE,{"derivedFrom":subQ1}),-1.0]])]});}
            var Q1;
            Q1=makeQuery(id+"F16.imprint","IMPRINT",FACE,{"disambiguationData":[TD([[makeQuery(id+"F16.imprint","IMPRINT",EDGE,{"derivedFrom":sQuery(id+"F16.wireOp",EDGE,"E89.MirrorCS")}),1.0]])]});
            var Q2;
            {var subQ10=sQuery(id+"F16.wireOp",EDGE,"E79.4");Q2=makeQuery(id+"F16.imprint","IMPRINT",FACE,{"disambiguationData":[TD([[makeQuery(id+"F16.imprint","IMPRINT",EDGE,{"derivedFrom":subQ10}),-1.0]])]});}
            var Q3;
            {var subQ4=sQuery(id+"F16.wireOp",EDGE,"E79.0");Q3=makeQuery(id+"F16.imprint","IMPRINT",FACE,{"disambiguationData":[TD([[makeQuery(id+"F16.imprint","IMPRINT",EDGE,{"derivedFrom":subQ4}),-1.0]])]});}
            var Q4;
            Q4=makeQuery(id+"F2.opExtrude","CAP_FACE",FACE,{"disambiguationData":[OSD([sQuery(id+"F0.wireOp",EDGE,"E12"),sQuery(id+"F0.wireOp",EDGE,"E13"),sQuery(id+"F0.wireOp",EDGE,"E14"),sQuery(id+"F0.wireOp",EDGE,"E15"),sQuery(id+"F0.wireOp",EDGE,"E17.filletArc"),sQuery(id+"F0.wireOp",EDGE,"E18.filletArc"),sQuery(id+"F0.wireOp",EDGE,"E19.filletArc"),sQuery(id+"F0.wireOp",EDGE,"E20.filletArc"),sQuery(id+"F0.wireOp",EDGE,"E25.0"),sQuery(id+"F0.wireOp",EDGE,"E25.1"),sQuery(id+"F0.wireOp",EDGE,"E25.2"),sQuery(id+"F0.wireOp",EDGE,"E25.3"),sQuery(id+"F0.wireOp",EDGE,"E25.4"),sQuery(id+"F0.wireOp",EDGE,"E25.5"),sQuery(id+"F0.wireOp",EDGE,"E25.6"),sQuery(id+"F0.wireOp",EDGE,"E25.7")])],"isStart":false});
            extrude(context, id + "F17", {"entities" : qUnion([Q0, Q1, Q2, Q3]), "operationType" : NewBodyOperationType.ADD, "endBound" : BoundingType.UP_TO_SURFACE, "endBoundEntityFace" : qUnion([Q4]), "depth" : 25 * mm});
        }
    });
